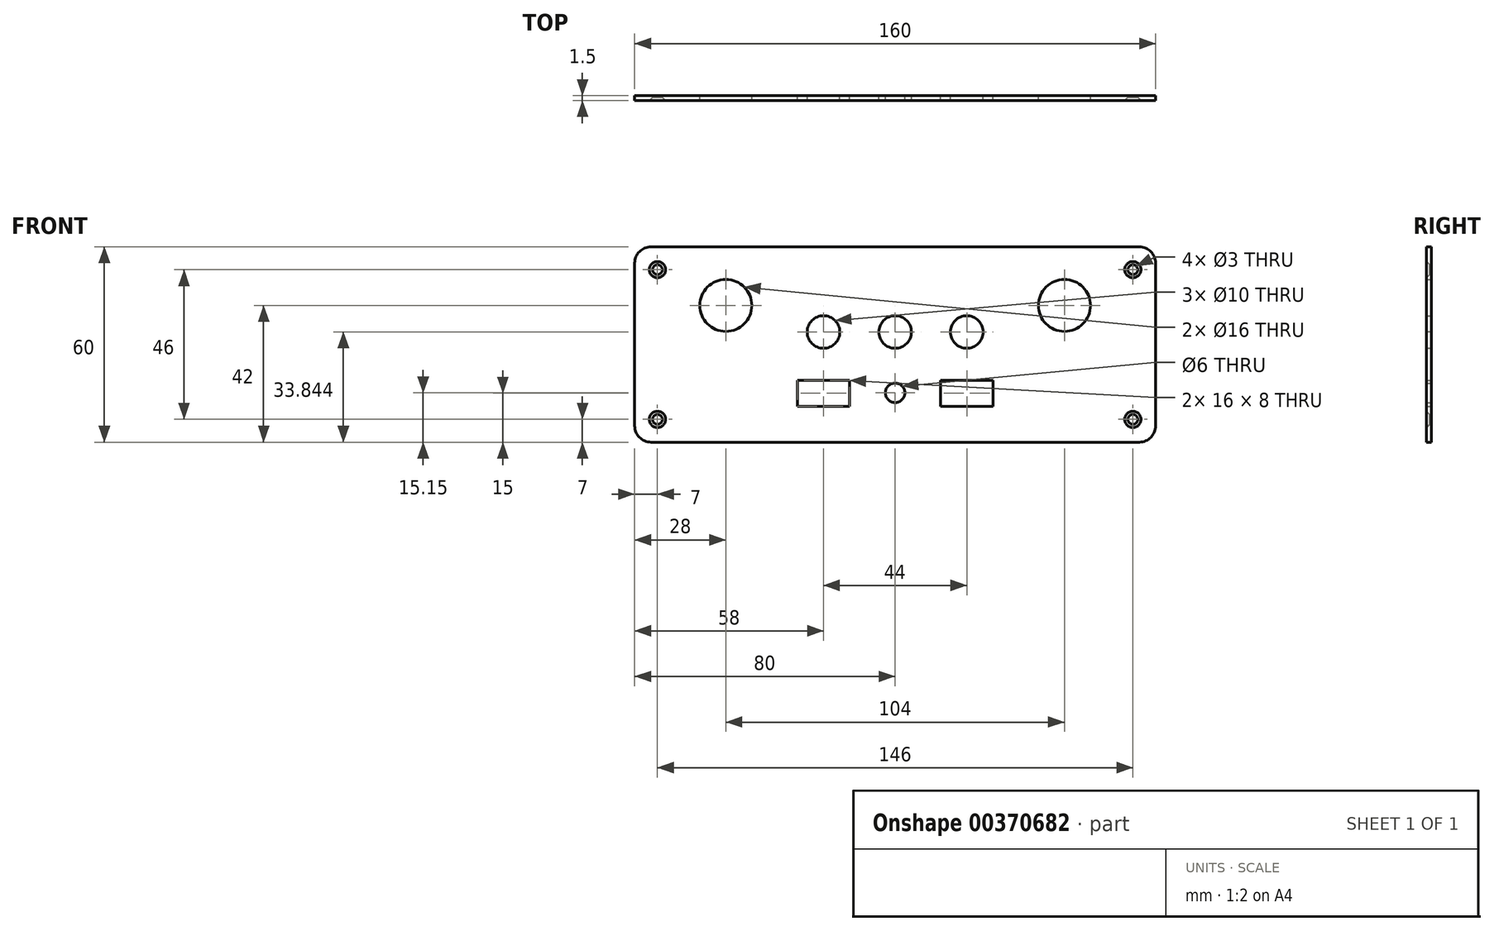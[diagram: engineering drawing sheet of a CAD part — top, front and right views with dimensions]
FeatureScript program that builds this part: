
annotation { "Feature Type Name" : "Feature", "Feature Type Description" : "" }
export const myFeature = defineFeature(function(context is Context, id is Id, definition is map)
    precondition{}
    {
        {
            var Q0;
            Q0=qCreatedBy(makeId("Front.planeOp"),FACE);
            var sketch = newSketch(context, id + "F0", { "sketchPlane" : qUnion([Q0])});
            skLineSegment(sketch, "E0.bottom", {"start": v(5, 0) * mm, "end": v(155, 0) * mm});
            skLineSegment(sketch, "E0.top", {"start": v(5, 60) * mm, "end": v(155, 60) * mm});
            skLineSegment(sketch, "E0.left", {"start": v(0, 5) * mm, "end": v(0, 55) * mm});
            skLineSegment(sketch, "E0.right", {"start": v(160, 5) * mm, "end": v(160, 55) * mm});
            skCircle(sketch, "E1", {"center": v(28, 42) * mm, "radius": 8 * mm});
            skCircle(sketch, "E2", {"center": v(132, 42) * mm, "radius": 8 * mm});
            skPoint(sketch, "E3.visualSharp", {"position": v(0, 60) * mm});
            skArc(sketch, "E3.filletArc", {"start": v(5, 60) * mm, "mid": v(1.46, 58.54) * mm, "end": v(0, 55) * mm});
            skPoint(sketch, "E4.visualSharp", {"position": v(0, 0) * mm});
            skArc(sketch, "E4.filletArc", {"start": v(0, 5) * mm, "mid": v(1.46, 1.46) * mm, "end": v(5, 0) * mm});
            skPoint(sketch, "E5.visualSharp", {"position": v(160, 0) * mm});
            skArc(sketch, "E5.filletArc", {"start": v(155, 0) * mm, "mid": v(158.54, 1.46) * mm, "end": v(160, 5) * mm});
            skPoint(sketch, "E6.visualSharp", {"position": v(160, 60) * mm});
            skArc(sketch, "E6.filletArc", {"start": v(160, 55) * mm, "mid": v(158.54, 58.54) * mm, "end": v(155, 60) * mm});
            skLineSegment(sketch, "E7.bottom", {"start": v(153, 7) * mm, "end": v(7, 7) * mm, "construction": true});
            skLineSegment(sketch, "E7.top", {"start": v(153, 53) * mm, "end": v(7, 53) * mm, "construction": true});
            skLineSegment(sketch, "E7.left", {"start": v(153, 17) * mm, "end": v(153, 53) * mm, "construction": true});
            skLineSegment(sketch, "E7.right", {"start": v(7, 7) * mm, "end": v(7, 53) * mm, "construction": true});
            skPoint(sketch, "E7.middle", {"position": v(80, 30) * mm});
            skCircle(sketch, "E8", {"center": v(7, 7) * mm, "radius": 1.5 * mm});
            skCircle(sketch, "E9", {"center": v(153, 53) * mm, "radius": 1.5 * mm});
            skCircle(sketch, "E10", {"center": v(153, 7) * mm, "radius": 1.5 * mm});
            skCircle(sketch, "E11", {"center": v(7, 53) * mm, "radius": 1.5 * mm});
            skLineSegment(sketch, "E12.bottom", {"start": v(110, 11) * mm, "end": v(94, 11) * mm});
            skLineSegment(sketch, "E12.top", {"start": v(110, 19) * mm, "end": v(94, 19) * mm});
            skLineSegment(sketch, "E12.left", {"start": v(110, 11) * mm, "end": v(110, 19) * mm});
            skLineSegment(sketch, "E12.right", {"start": v(94, 11) * mm, "end": v(94, 19) * mm});
            skPoint(sketch, "E12.middle", {"position": v(102, 15) * mm});
            skLineSegment(sketch, "E13.bottom", {"start": v(66, 11) * mm, "end": v(50, 11) * mm});
            skLineSegment(sketch, "E13.top", {"start": v(66, 19) * mm, "end": v(50, 19) * mm});
            skLineSegment(sketch, "E13.left", {"start": v(66, 11) * mm, "end": v(66, 19) * mm});
            skLineSegment(sketch, "E13.right", {"start": v(50, 11) * mm, "end": v(50, 19) * mm});
            skPoint(sketch, "E13.middle", {"position": v(58, 15) * mm});
            skLineSegment(sketch, "E14", {"start": v(7, 42) * mm, "end": v(153, 42) * mm, "construction": true});
            skCircle(sketch, "E15", {"center": v(58, 33.84) * mm, "radius": 5 * mm});
            skCircle(sketch, "E16", {"center": v(102, 33.84) * mm, "radius": 5 * mm});
            skCircle(sketch, "E17", {"center": v(80, 33.84) * mm, "radius": 5 * mm});
            skLineSegment(sketch, "E18", {"start": v(7, 15) * mm, "end": v(152.8, 15) * mm, "construction": true});
            skPoint(sketch, "E18.startSnap0", {"position": v(50, 15) * mm});
            skPoint(sketch, "E18.endSnap0", {"position": v(110, 15) * mm});
            skLineSegment(sketch, "E19", {"start": v(80, 60) * mm, "end": v(80, 0) * mm, "construction": true});
            skCircle(sketch, "E20", {"center": v(80, 15.15) * mm, "radius": 3 * mm});
            skLineSegment(sketch, "E21", {"start": v(153, 33.84) * mm, "end": v(7, 33.84) * mm, "construction": true});
            skSolve(sketch);
        }
        {
            var Q0;
            Q0 = qSketchRegion(id + "F0", true);
            extrude(context, id + "F1", {"entities" : qUnion([Q0]), "depth" : 1.5 * mm});
        }
        {
            var Q0;
            Q0=makeQuery(id+"F1.opExtrude","CAP_EDGE",EDGE,{"disambiguationData":[OSD([sQuery(id+"F0.wireOp",EDGE,"E9")])],"isStart":false});
            var Q1;
            Q1=makeQuery(id+"F1.opExtrude","CAP_EDGE",EDGE,{"disambiguationData":[OSD([sQuery(id+"F0.wireOp",EDGE,"E10")])],"isStart":false});
            var Q2;
            Q2=makeQuery(id+"F1.opExtrude","CAP_EDGE",EDGE,{"disambiguationData":[OSD([sQuery(id+"F0.wireOp",EDGE,"E11")])],"isStart":false});
            var Q3;
            Q3=makeQuery(id+"F1.opExtrude","CAP_EDGE",EDGE,{"disambiguationData":[OSD([sQuery(id+"F0.wireOp",EDGE,"E8")])],"isStart":false});
            chamfer(context, id + "F2", {"entities" : qUnion([Q0, Q1, Q2, Q3]), "width" : 1 * mm, "tangentPropagation" : true});
        }
    });
